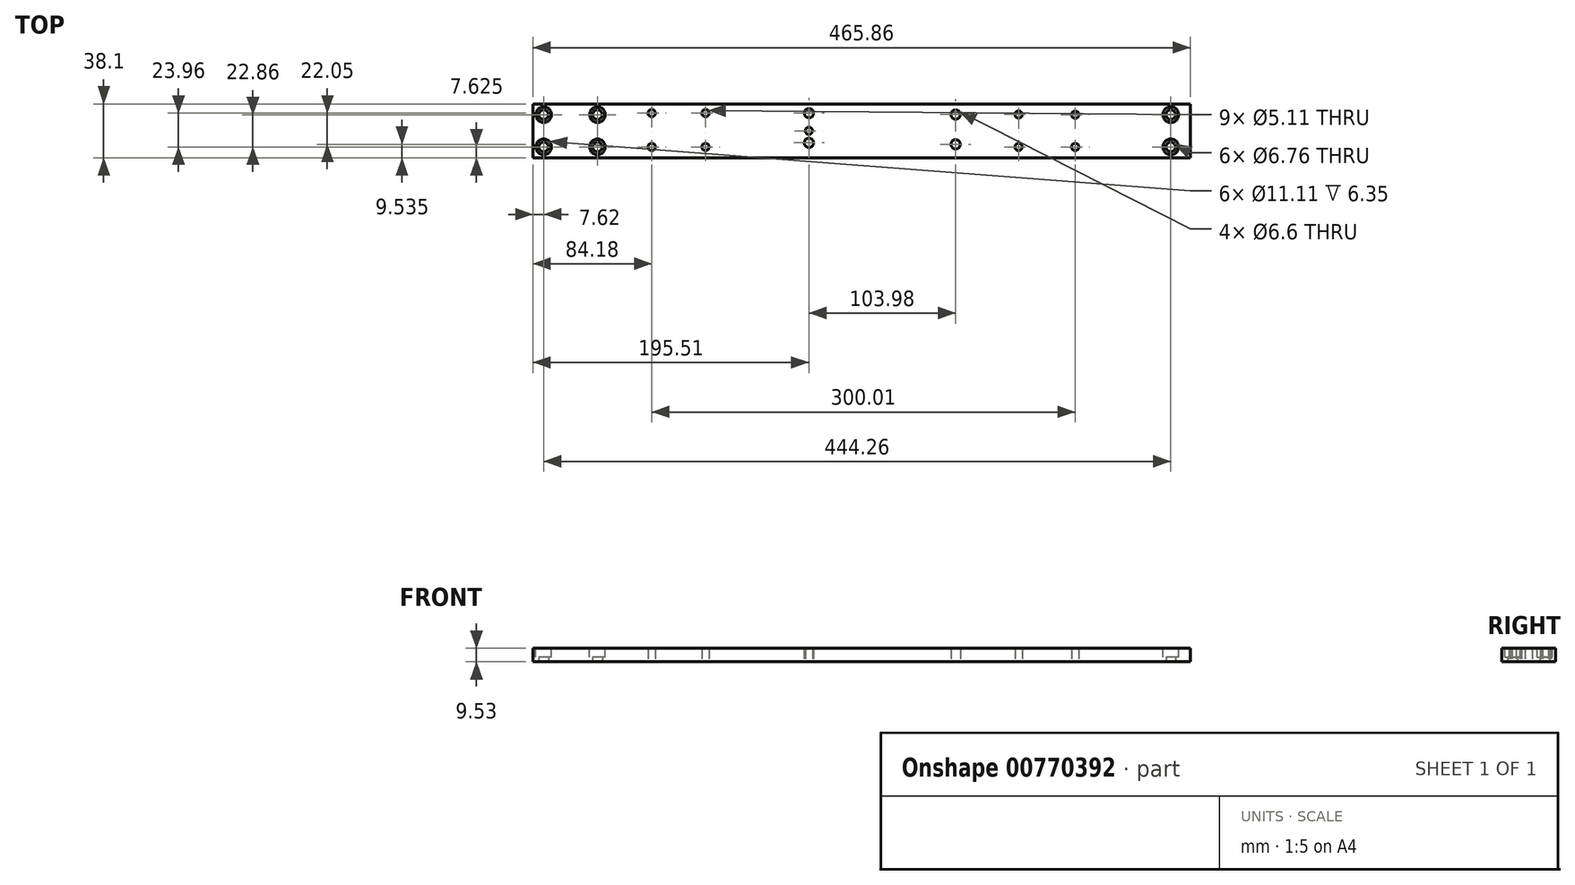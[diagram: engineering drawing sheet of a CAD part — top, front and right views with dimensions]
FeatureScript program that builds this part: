
annotation { "Feature Type Name" : "Feature", "Feature Type Description" : "" }
export const myFeature = defineFeature(function(context is Context, id is Id, definition is map)
    precondition{}
    {
        {
            var Q0;
            Q0=qCreatedBy(makeId("Top.planeOp"),FACE);
            var sketch = newSketch(context, id + "F0", { "sketchPlane" : qUnion([Q0])});
            skLineSegment(sketch, "E0.bottom", {"start": v(-524.78, -186.59) * mm, "end": v(-58.92, -186.59) * mm});
            skLineSegment(sketch, "E0.top", {"start": v(-524.78, -224.69) * mm, "end": v(-58.92, -224.69) * mm});
            skLineSegment(sketch, "E0.left", {"start": v(-524.78, -186.59) * mm, "end": v(-524.78, -224.69) * mm});
            skLineSegment(sketch, "E0.right", {"start": v(-58.92, -186.59) * mm, "end": v(-58.92, -224.69) * mm});
            skCircle(sketch, "E1", {"center": v(-517.16, -194.2) * mm, "radius": 3.38 * mm});
            skCircle(sketch, "E2", {"center": v(-479.06, -194.2) * mm, "radius": 3.38 * mm});
            skCircle(sketch, "E3", {"center": v(-479.06, -217.07) * mm, "radius": 3.38 * mm});
            skCircle(sketch, "E4", {"center": v(-517.16, -217.07) * mm, "radius": 3.38 * mm});
            skCircle(sketch, "E5", {"center": v(-72.9, -194.2) * mm, "radius": 3.38 * mm});
            skCircle(sketch, "E6", {"center": v(-72.9, -217.07) * mm, "radius": 3.38 * mm});
            skCircle(sketch, "E7", {"center": v(-440.6, -193.1) * mm, "radius": 2.56 * mm});
            skCircle(sketch, "E8", {"center": v(-440.6, -217.07) * mm, "radius": 2.56 * mm});
            skCircle(sketch, "E9", {"center": v(-402.5, -193.1) * mm, "radius": 2.56 * mm});
            skCircle(sketch, "E10", {"center": v(-402.5, -217.07) * mm, "radius": 2.56 * mm});
            skCircle(sketch, "E11", {"center": v(-180.69, -194.1) * mm, "radius": 2.56 * mm});
            skCircle(sketch, "E12", {"center": v(-140.59, -194.2) * mm, "radius": 2.56 * mm});
            skCircle(sketch, "E13", {"center": v(-180.69, -217.07) * mm, "radius": 2.56 * mm});
            skCircle(sketch, "E14", {"center": v(-140.59, -217.07) * mm, "radius": 2.56 * mm});
            skCircle(sketch, "E15", {"center": v(-329.27, -205.64) * mm, "radius": 2.56 * mm});
            skCircle(sketch, "E16", {"center": v(-329.27, -193.1) * mm, "radius": 3.3 * mm});
            skCircle(sketch, "E17", {"center": v(-329.27, -214.16) * mm, "radius": 3.3 * mm});
            skCircle(sketch, "E18", {"center": v(-225.29, -194.1) * mm, "radius": 3.3 * mm});
            skCircle(sketch, "E19", {"center": v(-225.29, -215.16) * mm, "radius": 3.3 * mm});
            skSolve(sketch);
        }
        {
            var Q0;
            Q0 = qSketchRegion(id + "F0", true);
            extrude(context, id + "F1", {"entities" : qUnion([Q0]), "depth" : 9.53 * mm, "offsetDistance" : 25 * mm});
        }
        {
            var Q0;
            Q0=makeQuery(id+"F1.opExtrude","CAP_FACE",FACE,{"disambiguationData":[OSD([sQuery(id+"F0.wireOp",EDGE,"E0.bottom"),sQuery(id+"F0.wireOp",EDGE,"E0.top"),sQuery(id+"F0.wireOp",EDGE,"E0.left"),sQuery(id+"F0.wireOp",EDGE,"E0.right"),sQuery(id+"F0.wireOp",EDGE,"E1"),sQuery(id+"F0.wireOp",EDGE,"E2"),sQuery(id+"F0.wireOp",EDGE,"E3"),sQuery(id+"F0.wireOp",EDGE,"E4"),sQuery(id+"F0.wireOp",EDGE,"E5"),sQuery(id+"F0.wireOp",EDGE,"E6"),sQuery(id+"F0.wireOp",EDGE,"E7"),sQuery(id+"F0.wireOp",EDGE,"E8"),sQuery(id+"F0.wireOp",EDGE,"E9"),sQuery(id+"F0.wireOp",EDGE,"E10"),sQuery(id+"F0.wireOp",EDGE,"E11"),sQuery(id+"F0.wireOp",EDGE,"E12"),sQuery(id+"F0.wireOp",EDGE,"E13"),sQuery(id+"F0.wireOp",EDGE,"E14"),sQuery(id+"F0.wireOp",EDGE,"E15"),sQuery(id+"F0.wireOp",EDGE,"E16"),sQuery(id+"F0.wireOp",EDGE,"E17"),sQuery(id+"F0.wireOp",EDGE,"E18"),sQuery(id+"F0.wireOp",EDGE,"E19")])],"isStart":false});
            var sketch = newSketch(context, id + "F2", { "sketchPlane" : qUnion([Q0])});
            skCircle(sketch, "E20", {"center": v(-517.16, -194.2) * mm, "radius": 5.55 * mm});
            skCircle(sketch, "E21", {"center": v(-517.16, -217.07) * mm, "radius": 5.55 * mm});
            skCircle(sketch, "E22", {"center": v(-479.06, -194.2) * mm, "radius": 5.55 * mm});
            skCircle(sketch, "E23", {"center": v(-479.06, -217.07) * mm, "radius": 5.55 * mm});
            skCircle(sketch, "E24", {"center": v(-72.9, -194.2) * mm, "radius": 5.55 * mm});
            skCircle(sketch, "E25", {"center": v(-72.9, -217.07) * mm, "radius": 5.55 * mm});
            skSolve(sketch);
        }
        {
            var Q0;
            Q0 = qSketchRegion(id + "F2", true);
            extrude(context, id + "F3", {"entities" : qUnion([Q0]), "operationType" : NewBodyOperationType.REMOVE, "oppositeDirection" : true, "depth" : 6.35 * mm, "offsetDistance" : 25 * mm});
        }
    });
